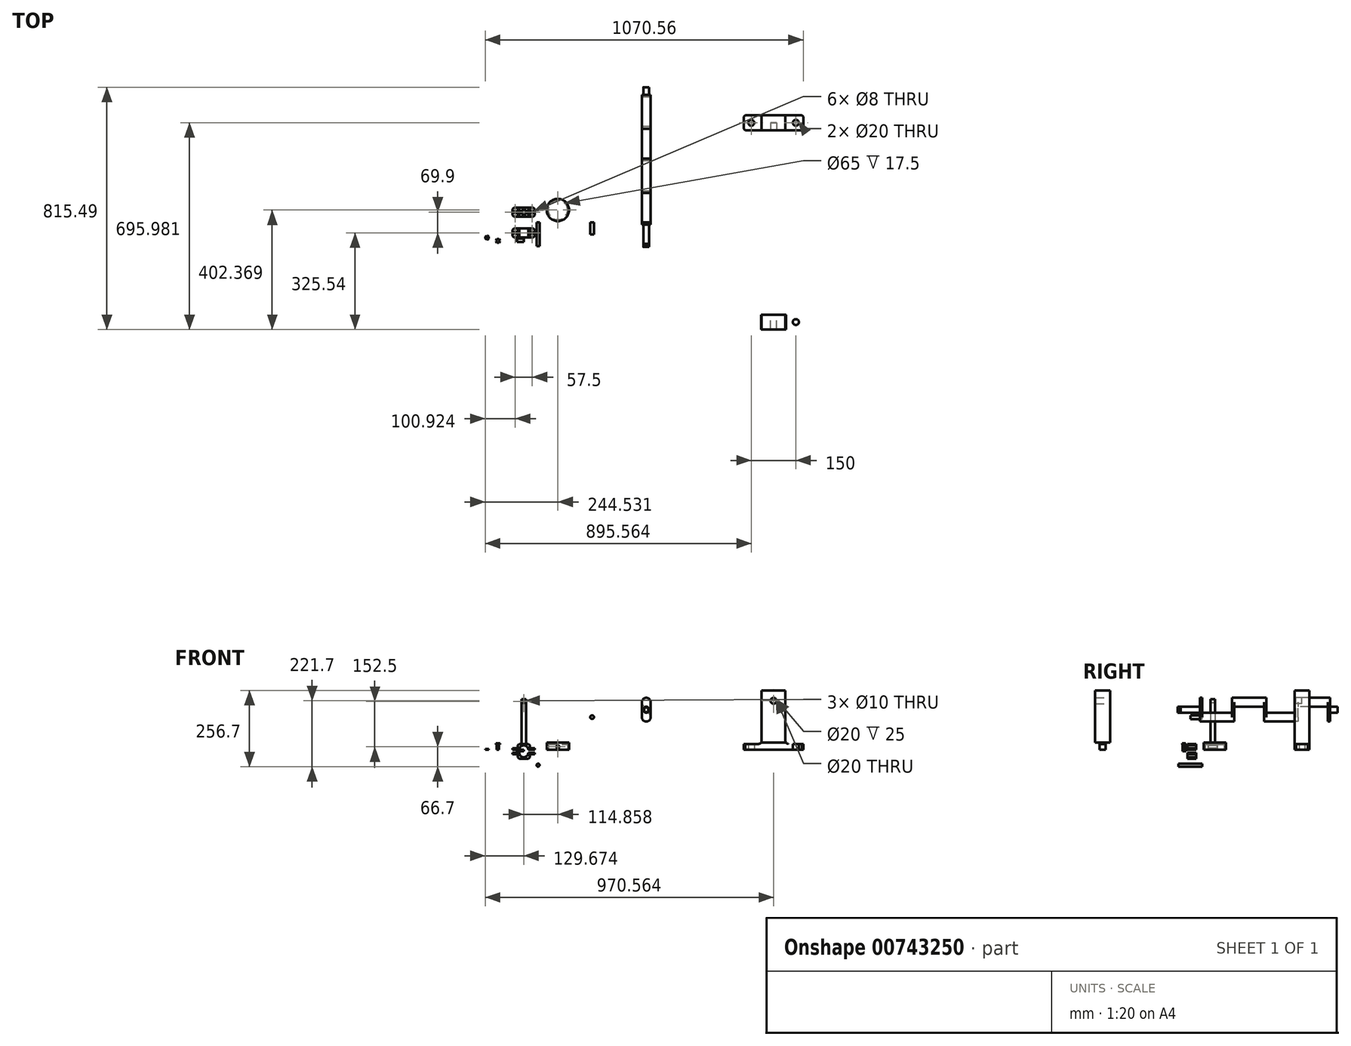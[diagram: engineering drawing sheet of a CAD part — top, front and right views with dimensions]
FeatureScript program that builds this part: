
annotation { "Feature Type Name" : "Feature", "Feature Type Description" : "" }
export const myFeature = defineFeature(function(context is Context, id is Id, definition is map)
    precondition{}
    {
        {
            var Q0;
            Q0=qCreatedBy(makeId("Top.planeOp"),FACE);
            var sketch = newSketch(context, id + "F0", { "sketchPlane" : qUnion([Q0])});
            skLineSegment(sketch, "E0.bottom", {"start": v(-66.46, 49.95) * mm, "end": v(8.54, 49.95) * mm});
            skLineSegment(sketch, "E0.top", {"start": v(-66.46, 19.95) * mm, "end": v(8.54, 19.95) * mm});
            skLineSegment(sketch, "E0.left", {"start": v(-66.46, 49.95) * mm, "end": v(-66.46, 19.95) * mm});
            skLineSegment(sketch, "E0.right", {"start": v(8.54, 49.95) * mm, "end": v(8.54, 19.95) * mm});
            skLineSegment(sketch, "E1", {"start": v(-48.96, 49.95) * mm, "end": v(-48.96, 19.95) * mm});
            skLineSegment(sketch, "E2.MirrorCS", {"start": v(-8.96, 49.95) * mm, "end": v(-8.96, 19.95) * mm});
            skPoint(sketch, "E3.start.orphan", {"position": v(-28.96, 49.95) * mm});
            skCircle(sketch, "E4", {"center": v(-57.7, 34.95) * mm, "radius": 4 * mm});
            skPoint(sketch, "E5.orphan", {"position": v(-48.96, 34.95) * mm});
            skPoint(sketch, "E6.start.orphan", {"position": v(-66.46, 34.95) * mm});
            skLineSegment(sketch, "E7", {"start": v(-28.96, 49.95) * mm, "end": v(-28.96, 38.42) * mm});
            skCircle(sketch, "E8.MirrorC", {"center": v(-0.2, 34.95) * mm, "radius": 4 * mm});
            skSolve(sketch);
        }
        {
            var Q0;
            {var subQ0=sQuery(id+"F0.wireOp",EDGE,"E1");Q0=makeQuery(id+"F0.imprint","IMPRINT",FACE,{"disambiguationData":[TD([[makeQuery(id+"F0.imprint","IMPRINT",EDGE,{"derivedFrom":subQ0}),1.0]])]});}
            extrude(context, id + "F1", {"entities" : qUnion([Q0]), "depth" : 20 * mm, "offsetDistance" : 25 * mm});
        }
        {
            var Q0;
            Q0 = qSketchRegion(id + "F0", true);
            var Q1;
            Q1=makeQuery(id+"F1.opExtrude","CAP_FACE",FACE,{"disambiguationData":[OSD([sQuery(id+"F0.wireOp",EDGE,"E0.bottom"),sQuery(id+"F0.wireOp",EDGE,"E0.top"),sQuery(id+"F0.wireOp",EDGE,"E1"),sQuery(id+"F0.wireOp",EDGE,"E2.MirrorCS")])],"isStart":true});
            extrude(context, id + "F2", {"entities" : qUnion([Q0, Q1]), "operationType" : NewBodyOperationType.ADD, "depth" : 5 * mm, "offsetDistance" : 25 * mm});
        }
        {
            var Q0;
            {var subQ0=sQuery(id+"F0.wireOp",EDGE,"E0.top");var subQ2=makeQuery(id+"F0.imprint","INTERSECT",VERTEX,{"derivedFrom":[subQ0,sQuery(id+"F0.wireOp",EDGE,"E1")]});Q0=makeQuery(id+"F2.boolean.opBoolean","MERGE",FACE,{"derivedFrom":[makeQuery(id+"F1.opExtrude","SWEPT_FACE",FACE,{"disambiguationData":[OSD([subQ0])]}),makeQuery(id+"F2.opExtrude","SWEPT_FACE",FACE,{"disambiguationData":[OSD([subQ0]),TDD([makeQuery(id+"F0.imprint","IMPRINT",EDGE,{"disambiguationData":[TD([[makeQuery(id+"F0.imprint","INTERSECT",VERTEX,{"derivedFrom":[subQ0,sQuery(id+"F0.wireOp",EDGE,"E0.left")]}),-1.0]])],"derivedFrom":subQ0}),makeQuery(id+"F0.imprint","IMPRINT",EDGE,{"disambiguationData":[TD([[subQ2,-1.0]])],"derivedFrom":subQ0}),makeQuery(id+"F0.imprint","IMPRINT",EDGE,{"disambiguationData":[TD([[makeQuery(id+"F0.imprint","INTERSECT",VERTEX,{"derivedFrom":[subQ0,sQuery(id+"F0.wireOp",EDGE,"E0.right")]}),1.0]])],"derivedFrom":subQ0})])]})]});}
            var sketch = newSketch(context, id + "F3", { "sketchPlane" : qUnion([Q0])});
            skLineSegment(sketch, "E9", {"start": v(-28.96, 0) * mm, "end": v(-43.96, 0) * mm});
            skLineSegment(sketch, "E10", {"start": v(-28.96, 0) * mm, "end": v(-28.96, 15) * mm});
            skArc(sketch, "E11", {"start": v(-28.96, 15) * mm, "mid": v(-39.56, 10.6) * mm, "end": v(-43.96, 0) * mm});
            skArc(sketch, "E12.MirrorCS", {"start": v(-28.96, 15) * mm, "mid": v(-18.35, 10.6) * mm, "end": v(-13.96, 0) * mm});
            skSolve(sketch);
        }
        {
            var Q0;
            Q0=makeQuery(id+"F3.imprint","IMPRINT",FACE,{"disambiguationData":[TD([[makeQuery(id+"F3.imprint","IMPRINT",EDGE,{"derivedFrom":sQuery(id+"F3.wireOp",EDGE,"E9")}),1.0]])]});
            var Q1;
            {var subQ0=sQuery(id+"F3.wireOp",EDGE,"E10");Q1=makeQuery(id+"F3.imprint","IMPRINT",FACE,{"disambiguationData":[TD([[makeQuery(id+"F3.imprint","IMPRINT",EDGE,{"derivedFrom":subQ0}),-1.0]])]});}
            extrude(context, id + "F4", {"entities" : qUnion([Q0, Q1]), "operationType" : NewBodyOperationType.REMOVE, "oppositeDirection" : true, "depth" : 46.2 * mm, "offsetDistance" : 25 * mm});
        }
        {
            var Q0;
            Q0=makeQuery(id+"F2.boolean.opBoolean","INTERSECT",EDGE,{"derivedFrom":[makeQuery(id+"F1.opExtrude","SWEPT_FACE",FACE,{"disambiguationData":[OSD([sQuery(id+"F0.wireOp",EDGE,"E1")])]}),makeQuery(id+"F2.opExtrude","CAP_FACE",FACE,{"disambiguationData":[OSD([sQuery(id+"F0.wireOp",EDGE,"E0.bottom"),sQuery(id+"F0.wireOp",EDGE,"E0.top"),sQuery(id+"F0.wireOp",EDGE,"E0.left"),sQuery(id+"F0.wireOp",EDGE,"E0.right"),sQuery(id+"F0.wireOp",EDGE,"E4"),sQuery(id+"F0.wireOp",EDGE,"E8.MirrorC")])],"isStart":false})]});
            var Q1;
            Q1=makeQuery(id+"F2.boolean.opBoolean","INTERSECT",EDGE,{"derivedFrom":[makeQuery(id+"F1.opExtrude","SWEPT_FACE",FACE,{"disambiguationData":[OSD([sQuery(id+"F0.wireOp",EDGE,"E2.MirrorCS")])]}),makeQuery(id+"F2.opExtrude","CAP_FACE",FACE,{"disambiguationData":[OSD([sQuery(id+"F0.wireOp",EDGE,"E0.bottom"),sQuery(id+"F0.wireOp",EDGE,"E0.top"),sQuery(id+"F0.wireOp",EDGE,"E0.left"),sQuery(id+"F0.wireOp",EDGE,"E0.right"),sQuery(id+"F0.wireOp",EDGE,"E4"),sQuery(id+"F0.wireOp",EDGE,"E8.MirrorC")])],"isStart":false})]});
            fillet(context, id + "F5", {"entities" : qUnion([Q0, Q1]), "radius" : 3 * mm, "tangentPropagation" : true, "allowEdgeOverflow" : false});
        }
        {
            var Q0;
            Q0=makeQuery(id+"F1.opExtrude","CAP_EDGE",EDGE,{"disambiguationData":[OSD([sQuery(id+"F0.wireOp",EDGE,"E2.MirrorCS")])],"isStart":false});
            var Q1;
            Q1=makeQuery(id+"F1.opExtrude","CAP_EDGE",EDGE,{"disambiguationData":[OSD([sQuery(id+"F0.wireOp",EDGE,"E1")])],"isStart":false});
            chamfer(context, id + "F6", {"entities" : qUnion([Q0, Q1]), "width" : 5 * mm, "tangentPropagation" : true});
        }
        {
            var Q0;
            Q0=makeQuery(id+"F2.opExtrude","SWEPT_EDGE",EDGE,{"disambiguationData":[OSD([sQuery(id+"F0.wireOp",EDGE,"E0.top"),sQuery(id+"F0.wireOp",EDGE,"E0.left")])]});
            var Q1;
            Q1=makeQuery(id+"F2.opExtrude","SWEPT_EDGE",EDGE,{"disambiguationData":[OSD([sQuery(id+"F0.wireOp",EDGE,"E0.bottom"),sQuery(id+"F0.wireOp",EDGE,"E0.left")])]});
            var Q2;
            Q2=makeQuery(id+"F2.opExtrude","SWEPT_EDGE",EDGE,{"disambiguationData":[OSD([sQuery(id+"F0.wireOp",EDGE,"E0.bottom"),sQuery(id+"F0.wireOp",EDGE,"E0.right")])]});
            var Q3;
            Q3=makeQuery(id+"F2.opExtrude","SWEPT_EDGE",EDGE,{"disambiguationData":[OSD([sQuery(id+"F0.wireOp",EDGE,"E0.top"),sQuery(id+"F0.wireOp",EDGE,"E0.right")])]});
            chamfer(context, id + "F7", {"entities" : qUnion([Q0, Q1, Q2, Q3]), "width" : 5 * mm, "tangentPropagation" : true});
        }
        {
            var Q0;
            Q0=makeQuery(id+"F1.opExtrude","SWEPT_BODY",BODY,{"disambiguationData":[OSD([sQuery(id+"F0.wireOp",EDGE,"E0.bottom"),sQuery(id+"F0.wireOp",EDGE,"E0.top"),sQuery(id+"F0.wireOp",EDGE,"E1"),sQuery(id+"F0.wireOp",EDGE,"E2.MirrorCS")])]});
            var Q1;
            Q1=qCreatedBy(makeId("Front.planeOp"),FACE);
            mirror(context, id + "F8", {"entities" : qUnion([Q0]), "mirrorPlane" : qUnion([Q1])});
        }
        {
            var Q0;
            Q0=makeQuery(id+"F1.opExtrude","CAP_FACE",FACE,{"disambiguationData":[OSD([sQuery(id+"F0.wireOp",EDGE,"E0.bottom"),sQuery(id+"F0.wireOp",EDGE,"E0.top"),sQuery(id+"F0.wireOp",EDGE,"E1"),sQuery(id+"F0.wireOp",EDGE,"E2.MirrorCS")])],"isStart":false});
            var sketch = newSketch(context, id + "F9", { "sketchPlane" : qUnion([Q0])});
            skLineSegment(sketch, "E13", {"start": v(-43.96, 34.95) * mm, "end": v(-13.96, 34.95) * mm});
            skCircle(sketch, "E14.cCircle", {"center": v(-28.96, 34.95) * mm, "radius": 7.5 * mm, "construction": true});
            skLineSegment(sketch, "E14.0", {"start": v(-36.46, 27.45) * mm, "end": v(-36.46, 42.45) * mm});
            skLineSegment(sketch, "E14.1", {"start": v(-36.46, 42.45) * mm, "end": v(-21.46, 42.45) * mm});
            skLineSegment(sketch, "E14.2", {"start": v(-21.46, 42.45) * mm, "end": v(-21.46, 27.45) * mm});
            skLineSegment(sketch, "E14.3", {"start": v(-21.46, 27.45) * mm, "end": v(-36.46, 27.45) * mm});
            skPoint(sketch, "E14.0.midPoint", {"position": v(-36.46, 34.95) * mm});
            skSolve(sketch);
        }
        {
            var Q0;
            {var subQ5=sQuery(id+"F9.wireOp",EDGE,"E14.3");Q0=makeQuery(id+"F9.imprint","IMPRINT",FACE,{"disambiguationData":[TD([[makeQuery(id+"F9.imprint","IMPRINT",EDGE,{"derivedFrom":subQ5}),-1.0]])]});}
            var Q1;
            {var subQ5=sQuery(id+"F9.wireOp",EDGE,"E14.1");Q1=makeQuery(id+"F9.imprint","IMPRINT",FACE,{"disambiguationData":[TD([[makeQuery(id+"F9.imprint","IMPRINT",EDGE,{"derivedFrom":subQ5}),-1.0]])]});}
            extrude(context, id + "F10", {"entities" : qUnion([Q0, Q1]), "operationType" : NewBodyOperationType.ADD, "depth" : 150 * mm, "offsetDistance" : 25 * mm});
        }
        {
            var Q0;
            Q0=makeQuery(id+"F10.opExtrude","SWEPT_FACE",FACE,{"disambiguationData":[OSD([sQuery(id+"F9.wireOp",EDGE,"E14.3")])]});
            var sketch = newSketch(context, id + "F11", { "sketchPlane" : qUnion([Q0])});
            skLineSegment(sketch, "E15", {"start": v(-28.96, 170) * mm, "end": v(-28.96, 162.5) * mm});
            skCircle(sketch, "E16", {"center": v(-28.96, 162.5) * mm, "radius": 5 * mm});
            skSolve(sketch);
        }
        {
            var Q0;
            Q0=makeQuery(id+"F11.imprint","IMPRINT",FACE,{"disambiguationData":[TD([[makeQuery(id+"F11.imprint","IMPRINT",EDGE,{"derivedFrom":sQuery(id+"F11.wireOp",EDGE,"E16")}),1.0]])]});
            extrude(context, id + "F12", {"entities" : qUnion([Q0]), "operationType" : NewBodyOperationType.REMOVE, "oppositeDirection" : true, "depth" : 25 * mm, "offsetDistance" : 25 * mm});
        }
        {
            var Q0;
            Q0=qCreatedBy(makeId("Top.planeOp"),FACE);
            var sketch = newSketch(context, id + "F13", { "sketchPlane" : qUnion([Q0])});
            skCircle(sketch, "E17", {"center": v(85.9, 41.88) * mm, "radius": 37.5 * mm});
            skSolve(sketch);
        }
        {
            var Q0;
            Q0=makeQuery(id+"F13.imprint","IMPRINT",FACE,{"disambiguationData":[TD([[makeQuery(id+"F13.imprint","IMPRINT",EDGE,{"derivedFrom":sQuery(id+"F13.wireOp",EDGE,"E17")}),1.0]])]});
            extrude(context, id + "F14", {"entities" : qUnion([Q0]), "depth" : 25 * mm, "offsetDistance" : 25 * mm});
        }
        {
            var Q0;
            Q0=makeQuery(id+"F14.opExtrude","CAP_FACE",FACE,{"disambiguationData":[OSD([sQuery(id+"F13.wireOp",EDGE,"E17")])],"isStart":true});
            var sketch = newSketch(context, id + "F15", { "sketchPlane" : qUnion([Q0])});
            skCircle(sketch, "E18", {"center": v(85.9, -41.88) * mm, "radius": 32.5 * mm});
            skSolve(sketch);
        }
        {
            var Q0;
            Q0=makeQuery(id+"F15.imprint","IMPRINT",FACE,{"disambiguationData":[TD([[makeQuery(id+"F15.imprint","IMPRINT",EDGE,{"derivedFrom":sQuery(id+"F15.wireOp",EDGE,"E18")}),1.0]])]});
            extrude(context, id + "F16", {"entities" : qUnion([Q0]), "operationType" : NewBodyOperationType.REMOVE, "oppositeDirection" : true, "depth" : 17.5 * mm, "offsetDistance" : 25 * mm});
        }
        {
            var Q0;
            Q0=makeQuery(id+"F16.boolean.opBoolean","COPY",FACE,{"derivedFrom":makeQuery(id+"F16.opExtrude","CAP_FACE",FACE,{"disambiguationData":[OSD([sQuery(id+"F15.wireOp",EDGE,"E18")])],"isStart":false})});
            var sketch = newSketch(context, id + "F17", { "sketchPlane" : qUnion([Q0])});
            skLineSegment(sketch, "E19.0", {"start": v(97.9, -53.88) * mm, "end": v(73.9, -53.88) * mm});
            skLineSegment(sketch, "E19.1", {"start": v(73.9, -53.88) * mm, "end": v(73.9, -29.88) * mm});
            skLineSegment(sketch, "E19.2", {"start": v(73.9, -29.88) * mm, "end": v(97.9, -29.88) * mm});
            skLineSegment(sketch, "E19.3", {"start": v(97.9, -29.88) * mm, "end": v(97.9, -53.88) * mm});
            skPoint(sketch, "E19.0.midPoint", {"position": v(85.9, -53.88) * mm});
            skPoint(sketch, "E19.cCircle.center.orphan", {"position": v(85.9, -41.88) * mm});
            skSolve(sketch);
        }
        {
            var Q0;
            Q0 = qSketchRegion(id + "F17", true);
            extrude(context, id + "F18", {"entities" : qUnion([Q0]), "operationType" : NewBodyOperationType.ADD, "depth" : 15 * mm, "offsetDistance" : 25 * mm});
        }
        {
            var Q0;
            Q0=makeQuery(id+"F18.opExtrude","SWEPT_FACE",FACE,{"disambiguationData":[OSD([sQuery(id+"F17.wireOp",EDGE,"E19.0")])]});
            var sketch = newSketch(context, id + "F19", { "sketchPlane" : qUnion([Q0])});
            skLineSegment(sketch, "E20", {"start": v(-85.9, 2.5) * mm, "end": v(-85.9, 17.5) * mm});
            skCircle(sketch, "E21", {"center": v(-85.9, 10) * mm, "radius": 5 * mm});
            skSolve(sketch);
        }
        {
            var Q0;
            {var subQ0=sQuery(id+"F19.wireOp",EDGE,"E21");var subQ1=sQuery(id+"F19.wireOp",EDGE,"E20");var subQ2=makeQuery(id+"F19.imprint","INTERSECT",VERTEX,{"disambiguationData":[OD(0.0)],"derivedFrom":[subQ1,subQ0]});Q0=makeQuery(id+"F19.imprint","IMPRINT",FACE,{"disambiguationData":[TD([[makeQuery(id+"F19.imprint","IMPRINT",EDGE,{"disambiguationData":[TD([[subQ2,-1.0]])],"derivedFrom":subQ1}),1.0]])]});}
            var Q1;
            {var subQ0=sQuery(id+"F19.wireOp",EDGE,"E21");var subQ1=sQuery(id+"F19.wireOp",EDGE,"E20");var subQ2=makeQuery(id+"F19.imprint","INTERSECT",VERTEX,{"disambiguationData":[OD(0.0)],"derivedFrom":[subQ1,subQ0]});Q1=makeQuery(id+"F19.imprint","IMPRINT",FACE,{"disambiguationData":[TD([[makeQuery(id+"F19.imprint","IMPRINT",EDGE,{"disambiguationData":[TD([[subQ2,-1.0]])],"derivedFrom":subQ1}),-1.0]])]});}
            extrude(context, id + "F20", {"entities" : qUnion([Q0, Q1]), "operationType" : NewBodyOperationType.REMOVE, "oppositeDirection" : true, "depth" : 101.7 * mm, "offsetDistance" : 25 * mm});
        }
        {
            var Q0;
            Q0 = qSketchRegion(id + "F19", true);
            extrude(context, id + "F21", {"entities" : qUnion([Q0]), "operationType" : NewBodyOperationType.REMOVE, "oppositeDirection" : true, "depth" : -50 * mm, "offsetDistance" : 25 * mm});
        }
        {
            var Q0;
            Q0=makeQuery(id+"F18.opExtrude","SWEPT_FACE",FACE,{"disambiguationData":[OSD([sQuery(id+"F17.wireOp",EDGE,"E19.3")])]});
            var sketch = newSketch(context, id + "F22", { "sketchPlane" : qUnion([Q0])});
            skLineSegment(sketch, "E22.bottom", {"start": v(53.88, 2.5) * mm, "end": v(29.88, 2.5) * mm});
            skLineSegment(sketch, "E22.top", {"start": v(53.88, 17.5) * mm, "end": v(29.88, 17.5) * mm});
            skLineSegment(sketch, "E22.left", {"start": v(53.88, 2.5) * mm, "end": v(53.88, 17.5) * mm});
            skLineSegment(sketch, "E22.right", {"start": v(29.88, 2.5) * mm, "end": v(29.88, 17.5) * mm});
            skSolve(sketch);
        }
        {
            var Q0;
            Q0 = qSketchRegion(id + "F22", true);
            extrude(context, id + "F23", {"entities" : qUnion([Q0]), "operationType" : NewBodyOperationType.REMOVE, "oppositeDirection" : true, "depth" : 27.8 * mm, "offsetDistance" : 25 * mm});
        }
        {
            var Q0;
            Q0=qCreatedBy(makeId("Front.planeOp"),FACE);
            var sketch = newSketch(context, id + "F24", { "sketchPlane" : qUnion([Q0])});
            skCircle(sketch, "E23", {"center": v(19.1, -51.7) * mm, "radius": 5 * mm});
            skSolve(sketch);
        }
        {
            var Q0;
            Q0 = qSketchRegion(id + "F24", true);
            extrude(context, id + "F25", {"entities" : qUnion([Q0]), "depth" : 80 * mm, "offsetDistance" : 25 * mm});
        }
        {
            var Q0;
            Q0=qCreatedBy(makeId("Top.planeOp"),FACE);
            var sketch = newSketch(context, id + "F26", { "sketchPlane" : qUnion([Q0])});
            skCircle(sketch, "E24", {"center": v(-115.98, -62.01) * mm, "radius": 4 * mm});
            skLineSegment(sketch, "E25", {"start": v(-116.37, -51.4) * mm, "end": v(-136.85, -51.4) * mm});
            skLineSegment(sketch, "E26", {"start": v(-136.85, -51.4) * mm, "end": v(-136.85, -57.16) * mm});
            skPoint(sketch, "E27", {"position": v(-152.63, -51.4) * mm});
            skCircle(sketch, "E28", {"center": v(-152.63, -51.4) * mm, "radius": 4 * mm});
            skCircle(sketch, "E29.cCircle", {"center": v(-152.63, -51.4) * mm, "radius": 6 * mm, "construction": true});
            skLineSegment(sketch, "E29.0", {"start": v(-146.63, -47.93) * mm, "end": v(-146.63, -54.86) * mm});
            skLineSegment(sketch, "E29.1", {"start": v(-146.63, -54.86) * mm, "end": v(-152.63, -58.32) * mm});
            skLineSegment(sketch, "E29.2", {"start": v(-152.63, -58.32) * mm, "end": v(-158.63, -54.86) * mm});
            skLineSegment(sketch, "E29.3", {"start": v(-158.63, -54.86) * mm, "end": v(-158.63, -47.93) * mm});
            skLineSegment(sketch, "E29.4", {"start": v(-158.63, -47.93) * mm, "end": v(-152.63, -44.46) * mm});
            skLineSegment(sketch, "E29.5", {"start": v(-152.63, -44.46) * mm, "end": v(-146.63, -47.93) * mm});
            skPoint(sketch, "E29.0.midPoint", {"position": v(-146.63, -51.4) * mm});
            skSolve(sketch);
        }
        {
            var Q0;
            Q0=makeQuery(id+"F26.imprint","IMPRINT",FACE,{"disambiguationData":[TD([[makeQuery(id+"F26.imprint","IMPRINT",EDGE,{"derivedFrom":sQuery(id+"F26.wireOp",EDGE,"E24")}),1.0]])]});
            extrude(context, id + "F27", {"entities" : qUnion([Q0]), "depth" : 17.5 * mm, "offsetDistance" : 25 * mm});
        }
        {
            var Q0;
            Q0=makeQuery(id+"F27.opExtrude","CAP_FACE",FACE,{"disambiguationData":[OSD([sQuery(id+"F26.wireOp",EDGE,"E24")])],"isStart":false});
            var sketch = newSketch(context, id + "F28", { "sketchPlane" : qUnion([Q0])});
            skCircle(sketch, "E30.cCircle", {"center": v(-115.98, -62.01) * mm, "radius": 6 * mm, "construction": true});
            skLineSegment(sketch, "E30.0", {"start": v(-112.51, -68.01) * mm, "end": v(-119.44, -68.01) * mm});
            skLineSegment(sketch, "E30.1", {"start": v(-119.44, -68.01) * mm, "end": v(-122.9, -62.01) * mm});
            skLineSegment(sketch, "E30.2", {"start": v(-122.9, -62.01) * mm, "end": v(-119.44, -56.01) * mm});
            skLineSegment(sketch, "E30.3", {"start": v(-119.44, -56.01) * mm, "end": v(-112.51, -56.01) * mm});
            skLineSegment(sketch, "E30.4", {"start": v(-112.51, -56.01) * mm, "end": v(-109.05, -62.01) * mm});
            skLineSegment(sketch, "E30.5", {"start": v(-109.05, -62.01) * mm, "end": v(-112.51, -68.01) * mm});
            skPoint(sketch, "E30.0.midPoint", {"position": v(-115.98, -68.01) * mm});
            skSolve(sketch);
        }
        {
            var Q0;
            Q0=makeQuery(id+"F28.imprint","IMPRINT",FACE,{"disambiguationData":[TD([[makeQuery(id+"F28.imprint","IMPRINT",EDGE,{"derivedFrom":sQuery(id+"F28.wireOp",EDGE,"E30.0")}),-1.0]])]});
            var Q1;
            Q1=makeQuery(id+"F28.imprint","IMPRINT",FACE,{"disambiguationData":[TD([[makeQuery(id+"F28.imprint","IMPRINT",EDGE,{"derivedFrom":makeQuery(id+"F27.opExtrude","CAP_EDGE",EDGE,{"disambiguationData":[OSD([sQuery(id+"F26.wireOp",EDGE,"E24")])],"isStart":false})}),1.0]])]});
            extrude(context, id + "F29", {"entities" : qUnion([Q0, Q1]), "operationType" : NewBodyOperationType.ADD, "depth" : 4 * mm, "offsetDistance" : 25 * mm});
        }
        {
            var Q0;
            Q0=makeQuery(id+"F26.imprint","IMPRINT",FACE,{"disambiguationData":[TD([[makeQuery(id+"F26.imprint","IMPRINT",EDGE,{"derivedFrom":sQuery(id+"F26.wireOp",EDGE,"E28")}),-1.0]])]});
            extrude(context, id + "F30", {"entities" : qUnion([Q0]), "depth" : 3 * mm, "offsetDistance" : 25 * mm});
        }
        {
            var Q0;
            Q0=qCreatedBy(makeId("Top.planeOp"),FACE);
            var sketch = newSketch(context, id + "F31", { "sketchPlane" : qUnion([Q0])});
            skLineSegment(sketch, "E31.bottom", {"start": v(-51.99, -65.98) * mm, "end": v(-28.68, -65.98) * mm});
            skLineSegment(sketch, "E31.top", {"start": v(-51.99, -54.32) * mm, "end": v(-28.68, -54.32) * mm});
            skLineSegment(sketch, "E31.left", {"start": v(-51.99, -65.98) * mm, "end": v(-51.99, -54.32) * mm});
            skLineSegment(sketch, "E31.right", {"start": v(-28.68, -65.98) * mm, "end": v(-28.68, -54.32) * mm});
            skSolve(sketch);
        }
        {
            var Q0;
            Q0=makeQuery(id+"F31.imprint","IMPRINT",FACE,{"disambiguationData":[TD([[makeQuery(id+"F31.imprint","IMPRINT",EDGE,{"derivedFrom":sQuery(id+"F31.wireOp",EDGE,"E31.bottom")}),1.0]])]});
            extrude(context, id + "F32", {"entities" : qUnion([Q0]), "depth" : -5 * mm, "offsetDistance" : 25 * mm});
        }
        {
            var Q0;
            Q0=makeQuery(id+"F8.opPattern","COPY",BODY,{"derivedFrom":makeQuery(id+"F1.opExtrude","SWEPT_BODY",BODY,{"disambiguationData":[OSD([sQuery(id+"F0.wireOp",EDGE,"E0.bottom"),sQuery(id+"F0.wireOp",EDGE,"E0.top"),sQuery(id+"F0.wireOp",EDGE,"E1"),sQuery(id+"F0.wireOp",EDGE,"E2.MirrorCS")])]}),"instanceName":"1"});
            var Q1;
            Q1=makeQuery(id+"F32.opExtrude","CAP_FACE",FACE,{"disambiguationData":[OSD([sQuery(id+"F31.wireOp",EDGE,"E31.bottom"),sQuery(id+"F31.wireOp",EDGE,"E31.top"),sQuery(id+"F31.wireOp",EDGE,"E31.left"),sQuery(id+"F31.wireOp",EDGE,"E31.right")])],"isStart":false});
            mirror(context, id + "F33", {"entities" : qUnion([Q0]), "mirrorPlane" : qUnion([Q1])});
        }
        {
            var Q0;
            Q0=qCreatedBy(makeId("Front.planeOp"),FACE);
            var sketch = newSketch(context, id + "F34", { "sketchPlane" : qUnion([Q0])});
            skCircle(sketch, "E32", {"center": v(383.3, 110.18) * mm, "radius": 15 * mm});
            skLineSegment(sketch, "E33", {"start": v(383.3, 110.18) * mm, "end": v(398.3, 110.18) * mm});
            skLineSegment(sketch, "E34", {"start": v(398.3, 110.18) * mm, "end": v(398.3, 160.18) * mm});
            skLineSegment(sketch, "E35", {"start": v(383.3, 110.18) * mm, "end": v(383.3, 125.18) * mm});
            skLineSegment(sketch, "E36.MirrorCS", {"start": v(368.3, 110.18) * mm, "end": v(368.3, 160.18) * mm});
            skArc(sketch, "E37", {"start": v(398.3, 160.18) * mm, "mid": v(383.3, 175.18) * mm, "end": v(368.3, 160.18) * mm});
            skSolve(sketch);
        }
        {
            var Q0;
            Q0 = qSketchRegion(id + "F34", true);
            extrude(context, id + "F35", {"entities" : qUnion([Q0]), "depth" : 7.5 * mm, "offsetDistance" : 25 * mm});
        }
        {
            var Q0;
            Q0=makeQuery(id+"F35.opExtrude","CAP_FACE",FACE,{"disambiguationData":[OSD([sQuery(id+"F34.wireOp",EDGE,"E32"),sQuery(id+"F34.wireOp",EDGE,"E34"),sQuery(id+"F34.wireOp",EDGE,"E36.MirrorCS"),sQuery(id+"F34.wireOp",EDGE,"E37")])],"isStart":true});
            var sketch = newSketch(context, id + "F36", { "sketchPlane" : qUnion([Q0])});
            skLineSegment(sketch, "E38", {"start": v(-383.3, 95.18) * mm, "end": v(-383.3, 110.18) * mm});
            skCircle(sketch, "E39", {"center": v(-383.3, 110.18) * mm, "radius": 15 * mm});
            skSolve(sketch);
        }
        {
            var Q0;
            Q0 = qSketchRegion(id + "F36", true);
            extrude(context, id + "F37", {"entities" : qUnion([Q0]), "operationType" : NewBodyOperationType.ADD, "depth" : 100 * mm, "offsetDistance" : 25 * mm});
        }
        {
            var Q0;
            Q0=makeQuery(id+"F37.opExtrude","CAP_FACE",FACE,{"disambiguationData":[OSD([sQuery(id+"F36.wireOp",EDGE,"E39")])],"isStart":false});
            var sketch = newSketch(context, id + "F38", { "sketchPlane" : qUnion([Q0])});
            skLineSegment(sketch, "E40", {"start": v(-383.3, 110.18) * mm, "end": v(-398.3, 110.18) * mm});
            skLineSegment(sketch, "E41", {"start": v(-398.3, 110.18) * mm, "end": v(-398.3, 160.18) * mm});
            skLineSegment(sketch, "E42", {"start": v(-383.3, 110.18) * mm, "end": v(-383.3, 125.18) * mm});
            skLineSegment(sketch, "E43.MirrorCS", {"start": v(-368.3, 110.18) * mm, "end": v(-368.3, 160.18) * mm});
            skArc(sketch, "E44", {"start": v(-368.3, 160.18) * mm, "mid": v(-383.3, 175.18) * mm, "end": v(-398.3, 160.18) * mm});
            skPoint(sketch, "E45.end.orphan", {"position": v(-367.15, 110.18) * mm});
            skArc(sketch, "E46", {"start": v(-398.3, 110.18) * mm, "mid": v(-383.3, 95.18) * mm, "end": v(-368.3, 110.18) * mm});
            skSolve(sketch);
        }
        {
            var Q0;
            Q0 = qSketchRegion(id + "F38", true);
            extrude(context, id + "F39", {"entities" : qUnion([Q0]), "operationType" : NewBodyOperationType.ADD, "depth" : 7.5 * mm, "offsetDistance" : 25 * mm});
        }
        {
            var Q0;
            Q0=makeQuery(id+"F39.opExtrude","CAP_FACE",FACE,{"disambiguationData":[OSD([sQuery(id+"F38.wireOp",EDGE,"E41"),sQuery(id+"F38.wireOp",EDGE,"E43.MirrorCS"),sQuery(id+"F38.wireOp",EDGE,"E44"),sQuery(id+"F38.wireOp",EDGE,"E46")])],"isStart":false});
            var sketch = newSketch(context, id + "F40", { "sketchPlane" : qUnion([Q0])});
            skCircle(sketch, "E47", {"center": v(-383.3, 160.18) * mm, "radius": 15 * mm});
            skSolve(sketch);
        }
        {
            var Q0;
            Q0 = qSketchRegion(id + "F40", true);
            extrude(context, id + "F41", {"entities" : qUnion([Q0]), "operationType" : NewBodyOperationType.ADD, "depth" : 100 * mm, "offsetDistance" : 25 * mm});
        }
        {
            var Q0;
            Q0=makeQuery(id+"F41.opExtrude","CAP_FACE",FACE,{"disambiguationData":[OSD([sQuery(id+"F40.wireOp",EDGE,"E47")])],"isStart":false});
            var sketch = newSketch(context, id + "F42", { "sketchPlane" : qUnion([Q0])});
            skLineSegment(sketch, "E48", {"start": v(-383.3, 160.18) * mm, "end": v(-398.3, 160.18) * mm});
            skLineSegment(sketch, "E49", {"start": v(-398.3, 160.18) * mm, "end": v(-398.3, 110.18) * mm});
            skLineSegment(sketch, "E50", {"start": v(-383.3, 160.18) * mm, "end": v(-383.3, 145.18) * mm});
            skLineSegment(sketch, "E51.MirrorCS", {"start": v(-368.3, 160.18) * mm, "end": v(-368.3, 110.18) * mm});
            skArc(sketch, "E52", {"start": v(-368.3, 160.18) * mm, "mid": v(-383.3, 175.18) * mm, "end": v(-398.3, 160.18) * mm});
            skArc(sketch, "E53", {"start": v(-398.3, 110.18) * mm, "mid": v(-383.3, 95.18) * mm, "end": v(-368.3, 110.18) * mm});
            skSolve(sketch);
        }
        {
            var Q0;
            {var subQ2=sQuery(id+"F42.wireOp",EDGE,"E49");Q0=makeQuery(id+"F42.imprint","IMPRINT",FACE,{"disambiguationData":[TD([[makeQuery(id+"F42.imprint","IMPRINT",EDGE,{"derivedFrom":subQ2}),1.0]])]});}
            var Q1;
            Q1=makeQuery(id+"F42.imprint","IMPRINT",FACE,{"disambiguationData":[TD([[makeQuery(id+"F42.imprint","IMPRINT",EDGE,{"derivedFrom":sQuery(id+"F42.wireOp",EDGE,"E48")}),-1.0]])]});
            var Q2;
            {var subQ0=sQuery(id+"F42.wireOp",EDGE,"E48");Q2=makeQuery(id+"F42.imprint","IMPRINT",FACE,{"disambiguationData":[TD([[makeQuery(id+"F42.imprint","IMPRINT",EDGE,{"derivedFrom":subQ0}),1.0]])]});}
            extrude(context, id + "F43", {"entities" : qUnion([Q0, Q1, Q2]), "operationType" : NewBodyOperationType.ADD, "depth" : 7.5 * mm, "offsetDistance" : 25 * mm});
        }
        {
            var Q0;
            Q0=makeQuery(id+"F43.opExtrude","CAP_FACE",FACE,{"disambiguationData":[OSD([sQuery(id+"F42.wireOp",EDGE,"E49"),sQuery(id+"F42.wireOp",EDGE,"E51.MirrorCS"),sQuery(id+"F42.wireOp",EDGE,"E52"),sQuery(id+"F42.wireOp",EDGE,"E53")])],"isStart":false});
            var sketch = newSketch(context, id + "F44", { "sketchPlane" : qUnion([Q0])});
            skCircle(sketch, "E54", {"center": v(-383.3, 110.18) * mm, "radius": 15 * mm});
            skSolve(sketch);
        }
        {
            var Q0;
            Q0 = qSketchRegion(id + "F44", true);
            extrude(context, id + "F45", {"entities" : qUnion([Q0]), "operationType" : NewBodyOperationType.ADD, "depth" : 100 * mm, "offsetDistance" : 25 * mm});
        }
        {
            var Q0;
            Q0=makeQuery(id+"F45.opExtrude","CAP_FACE",FACE,{"disambiguationData":[OSD([sQuery(id+"F44.wireOp",EDGE,"E54")])],"isStart":false});
            var sketch = newSketch(context, id + "F46", { "sketchPlane" : qUnion([Q0])});
            skLineSegment(sketch, "E55", {"start": v(-383.3, 110.18) * mm, "end": v(-398.3, 110.18) * mm});
            skLineSegment(sketch, "E56", {"start": v(-398.3, 110.18) * mm, "end": v(-398.3, 160.18) * mm});
            skLineSegment(sketch, "E57", {"start": v(-383.3, 110.18) * mm, "end": v(-383.3, 125.18) * mm});
            skLineSegment(sketch, "E58.MirrorCS", {"start": v(-368.3, 110.18) * mm, "end": v(-368.3, 160.18) * mm});
            skArc(sketch, "E59", {"start": v(-398.3, 110.18) * mm, "mid": v(-383.3, 95.18) * mm, "end": v(-368.3, 110.18) * mm});
            skArc(sketch, "E60", {"start": v(-368.3, 160.18) * mm, "mid": v(-383.3, 175.18) * mm, "end": v(-398.3, 160.18) * mm});
            skSolve(sketch);
        }
        {
            var Q0;
            Q0 = qSketchRegion(id + "F46", true);
            extrude(context, id + "F47", {"entities" : qUnion([Q0]), "operationType" : NewBodyOperationType.ADD, "depth" : 7.5 * mm, "offsetDistance" : 25 * mm});
        }
        {
            var Q0;
            Q0=makeQuery(id+"F47.opExtrude","CAP_FACE",FACE,{"disambiguationData":[OSD([sQuery(id+"F46.wireOp",EDGE,"E56"),sQuery(id+"F46.wireOp",EDGE,"E58.MirrorCS"),sQuery(id+"F46.wireOp",EDGE,"E59"),sQuery(id+"F46.wireOp",EDGE,"E60")])],"isStart":false});
            var sketch = newSketch(context, id + "F48", { "sketchPlane" : qUnion([Q0])});
            skCircle(sketch, "E61", {"center": v(-383.3, 160.18) * mm, "radius": 15 * mm});
            skSolve(sketch);
        }
        {
            var Q0;
            Q0 = qSketchRegion(id + "F48", true);
            extrude(context, id + "F49", {"entities" : qUnion([Q0]), "operationType" : NewBodyOperationType.ADD, "depth" : 100 * mm, "offsetDistance" : 25 * mm});
        }
        {
            var Q0;
            Q0=makeQuery(id+"F49.opExtrude","CAP_FACE",FACE,{"disambiguationData":[OSD([sQuery(id+"F48.wireOp",EDGE,"E61")])],"isStart":false});
            var sketch = newSketch(context, id + "F50", { "sketchPlane" : qUnion([Q0])});
            skLineSegment(sketch, "E62", {"start": v(-383.3, 160.18) * mm, "end": v(-398.3, 160.18) * mm});
            skLineSegment(sketch, "E63", {"start": v(-398.3, 160.18) * mm, "end": v(-398.3, 110.18) * mm});
            skLineSegment(sketch, "E64", {"start": v(-383.3, 160.18) * mm, "end": v(-383.3, 145.18) * mm});
            skLineSegment(sketch, "E65.MirrorCS", {"start": v(-368.3, 160.18) * mm, "end": v(-368.3, 110.18) * mm});
            skArc(sketch, "E66", {"start": v(-368.3, 160.18) * mm, "mid": v(-383.3, 175.18) * mm, "end": v(-398.3, 160.18) * mm});
            skArc(sketch, "E67", {"start": v(-398.3, 110.18) * mm, "mid": v(-383.3, 95.18) * mm, "end": v(-368.3, 110.18) * mm});
            skSolve(sketch);
        }
        {
            var Q0;
            {var subQ2=sQuery(id+"F50.wireOp",EDGE,"E63");Q0=makeQuery(id+"F50.imprint","IMPRINT",FACE,{"disambiguationData":[TD([[makeQuery(id+"F50.imprint","IMPRINT",EDGE,{"derivedFrom":subQ2}),1.0]])]});}
            var Q1;
            Q1=makeQuery(id+"F50.imprint","IMPRINT",FACE,{"disambiguationData":[TD([[makeQuery(id+"F50.imprint","IMPRINT",EDGE,{"derivedFrom":sQuery(id+"F50.wireOp",EDGE,"E62")}),-1.0]])]});
            var Q2;
            {var subQ0=sQuery(id+"F50.wireOp",EDGE,"E62");Q2=makeQuery(id+"F50.imprint","IMPRINT",FACE,{"disambiguationData":[TD([[makeQuery(id+"F50.imprint","IMPRINT",EDGE,{"derivedFrom":subQ0}),1.0]])]});}
            extrude(context, id + "F51", {"entities" : qUnion([Q0, Q1, Q2]), "operationType" : NewBodyOperationType.ADD, "depth" : 7.5 * mm, "offsetDistance" : 25 * mm});
        }
        {
            var Q0;
            Q0=makeQuery(id+"F51.opExtrude","CAP_FACE",FACE,{"disambiguationData":[OSD([sQuery(id+"F50.wireOp",EDGE,"E63"),sQuery(id+"F50.wireOp",EDGE,"E65.MirrorCS"),sQuery(id+"F50.wireOp",EDGE,"E66"),sQuery(id+"F50.wireOp",EDGE,"E67")])],"isStart":false});
            var sketch = newSketch(context, id + "F52", { "sketchPlane" : qUnion([Q0])});
            skLineSegment(sketch, "E68", {"start": v(-398.3, 135.18) * mm, "end": v(-393.3, 135.18) * mm});
            skCircle(sketch, "E69", {"center": v(-383.3, 135.18) * mm, "radius": 10 * mm});
            skLineSegment(sketch, "E70.trimOffspring", {"start": v(-373.3, 135.18) * mm, "end": v(-368.3, 135.18) * mm});
            skSolve(sketch);
        }
        {
            var Q0;
            {var subQ0=sQuery(id+"F52.wireOp",EDGE,"E69");var subQ1=makeQuery(id+"F52.imprint","INTERSECT",VERTEX,{"derivedFrom":[sQuery(id+"F52.wireOp",EDGE,"E68"),subQ0]});Q0=makeQuery(id+"F52.imprint","IMPRINT",FACE,{"disambiguationData":[TD([[makeQuery(id+"F52.imprint","IMPRINT",EDGE,{"disambiguationData":[TD([[subQ1,1.0]])],"derivedFrom":subQ0}),1.0]])]});}
            extrude(context, id + "F53", {"entities" : qUnion([Q0]), "operationType" : NewBodyOperationType.ADD, "depth" : 25 * mm, "offsetDistance" : 25 * mm});
        }
        {
            var Q0;
            Q0=makeQuery(id+"F35.opExtrude","CAP_FACE",FACE,{"disambiguationData":[OSD([sQuery(id+"F34.wireOp",EDGE,"E32"),sQuery(id+"F34.wireOp",EDGE,"E34"),sQuery(id+"F34.wireOp",EDGE,"E36.MirrorCS"),sQuery(id+"F34.wireOp",EDGE,"E37")])],"isStart":false});
            var sketch = newSketch(context, id + "F54", { "sketchPlane" : qUnion([Q0])});
            skLineSegment(sketch, "E71", {"start": v(368.3, 135.18) * mm, "end": v(373.3, 135.18) * mm});
            skCircle(sketch, "E72", {"center": v(383.3, 135.18) * mm, "radius": 10 * mm});
            skLineSegment(sketch, "E73.trimOffspring", {"start": v(383.3, 135.18) * mm, "end": v(398.3, 135.18) * mm});
            skSolve(sketch);
        }
        {
            var Q0;
            {var subQ0=sQuery(id+"F54.wireOp",EDGE,"E72");var subQ1=makeQuery(id+"F54.imprint","INTERSECT",VERTEX,{"derivedFrom":[sQuery(id+"F54.wireOp",EDGE,"E71"),subQ0]});Q0=makeQuery(id+"F54.imprint","IMPRINT",FACE,{"disambiguationData":[TD([[makeQuery(id+"F54.imprint","IMPRINT",EDGE,{"disambiguationData":[TD([[subQ1,1.0]])],"derivedFrom":subQ0}),1.0]])]});}
            extrude(context, id + "F55", {"entities" : qUnion([Q0]), "operationType" : NewBodyOperationType.ADD, "depth" : 75 * mm, "offsetDistance" : 25 * mm});
        }
        {
            var Q0;
            Q0=qCreatedBy(makeId("Top.planeOp"),FACE);
            var sketch = newSketch(context, id + "F56", { "sketchPlane" : qUnion([Q0])});
            skLineSegment(sketch, "E74.bottom", {"start": v(911.93, 310.5) * mm, "end": v(711.93, 310.5) * mm});
            skLineSegment(sketch, "E74.top", {"start": v(911.93, 360.5) * mm, "end": v(711.93, 360.5) * mm});
            skLineSegment(sketch, "E74.left", {"start": v(911.93, 310.5) * mm, "end": v(911.93, 360.5) * mm});
            skLineSegment(sketch, "E74.right", {"start": v(711.93, 310.5) * mm, "end": v(711.93, 360.5) * mm});
            skSolve(sketch);
        }
        {
            var Q0;
            Q0=makeQuery(id+"F56.imprint","IMPRINT",FACE,{"disambiguationData":[TD([[makeQuery(id+"F56.imprint","IMPRINT",EDGE,{"derivedFrom":sQuery(id+"F56.wireOp",EDGE,"E74.bottom")}),-1.0]])]});
            extrude(context, id + "F57", {"entities" : qUnion([Q0]), "depth" : 200 * mm, "offsetDistance" : 25 * mm});
        }
        {
            var Q0;
            Q0=makeQuery(id+"F57.opExtrude","SWEPT_FACE",FACE,{"disambiguationData":[OSD([sQuery(id+"F56.wireOp",EDGE,"E74.bottom")])]});
            var sketch = newSketch(context, id + "F58", { "sketchPlane" : qUnion([Q0])});
            skLineSegment(sketch, "E75", {"start": v(811.93, 200) * mm, "end": v(811.93, 165) * mm});
            skCircle(sketch, "E76", {"center": v(811.93, 165) * mm, "radius": 10 * mm});
            skSolve(sketch);
        }
        {
            var Q0;
            Q0 = qSketchRegion(id + "F58", true);
            extrude(context, id + "F59", {"entities" : qUnion([Q0]), "operationType" : NewBodyOperationType.REMOVE, "oppositeDirection" : true, "depth" : 25 * mm, "offsetDistance" : 25 * mm});
        }
        {
            var Q0;
            Q0=makeQuery(id+"F57.opExtrude","SWEPT_BODY",BODY,{"disambiguationData":[OSD([sQuery(id+"F56.wireOp",EDGE,"E74.bottom"),sQuery(id+"F56.wireOp",EDGE,"E74.top"),sQuery(id+"F56.wireOp",EDGE,"E74.left"),sQuery(id+"F56.wireOp",EDGE,"E74.right")])]});
            var Q1;
            Q1=qCreatedBy(makeId("Front.planeOp"),FACE);
            mirror(context, id + "F60", {"entities" : qUnion([Q0]), "mirrorPlane" : qUnion([Q1])});
        }
        {
            var Q0;
            Q0=makeQuery(id+"F55.opExtrude","CAP_FACE",FACE,{"disambiguationData":[OSD([sQuery(id+"F54.wireOp",EDGE,"E72")])],"isStart":false});
            var sketch = newSketch(context, id + "F61", { "sketchPlane" : qUnion([Q0])});
            skCircle(sketch, "E77", {"center": v(383.3, 135.18) * mm, "radius": 7.5 * mm});
            skLineSegment(sketch, "E78", {"start": v(383.3, 135.18) * mm, "end": v(383.3, 145.18) * mm});
            skLineSegment(sketch, "E79", {"start": v(383.3, 142.68) * mm, "end": v(382.3, 142.68) * mm});
            skLineSegment(sketch, "E80", {"start": v(382.3, 142.68) * mm, "end": v(381.34, 145) * mm});
            skLineSegment(sketch, "E81.MirrorCS", {"start": v(383.3, 142.68) * mm, "end": v(384.3, 142.68) * mm});
            skLineSegment(sketch, "E82.MirrorCS", {"start": v(384.3, 142.68) * mm, "end": v(385.26, 145) * mm});
            skSolve(sketch);
        }
        {
            var Q0;
            {var subQ3=sQuery(id+"F61.wireOp",EDGE,"E79");Q0=makeQuery(id+"F61.imprint","IMPRINT",FACE,{"disambiguationData":[TD([[makeQuery(id+"F61.imprint","IMPRINT",EDGE,{"derivedFrom":subQ3}),-1.0]])]});}
            var Q1;
            {var subQ3=sQuery(id+"F61.wireOp",EDGE,"E81.MirrorCS");Q1=makeQuery(id+"F61.imprint","IMPRINT",FACE,{"disambiguationData":[TD([[makeQuery(id+"F61.imprint","IMPRINT",EDGE,{"derivedFrom":subQ3}),1.0]])]});}
            extrude(context, id + "F62", {"entities" : qUnion([Q0, Q1]), "operationType" : NewBodyOperationType.REMOVE, "oppositeDirection" : true, "depth" : 10 * mm, "offsetDistance" : 25 * mm});
        }
        {
            var Q0;
            Q0=makeQuery(id+"F62.boolean.opBoolean","COPY",FACE,{"derivedFrom":makeQuery(id+"F62.opExtrude","SWEPT_FACE",FACE,{"disambiguationData":[OSD([sQuery(id+"F61.wireOp",EDGE,"E79"),sQuery(id+"F61.wireOp",EDGE,"E81.MirrorCS")])]})});
            var Q1;
            Q1=makeQuery(id+"F62.boolean.opBoolean","COPY",FACE,{"derivedFrom":makeQuery(id+"F62.opExtrude","SWEPT_FACE",FACE,{"disambiguationData":[OSD([sQuery(id+"F61.wireOp",EDGE,"E80")])]})});
            var Q2;
            Q2=makeQuery(id+"F62.boolean.opBoolean","COPY",FACE,{"derivedFrom":makeQuery(id+"F62.opExtrude","SWEPT_FACE",FACE,{"disambiguationData":[OSD([sQuery(id+"F61.wireOp",EDGE,"E82.MirrorCS")])]})});
            var Q3;
            Q3=makeQuery(id+"F62.boolean.opBoolean","COPY",FACE,{"derivedFrom":makeQuery(id+"F62.opExtrude","CAP_FACE",FACE,{"disambiguationData":[OSD([sQuery(id+"F54.wireOp",EDGE,"E72"),sQuery(id+"F61.wireOp",EDGE,"E79"),sQuery(id+"F61.wireOp",EDGE,"E80"),sQuery(id+"F61.wireOp",EDGE,"E81.MirrorCS"),sQuery(id+"F61.wireOp",EDGE,"E82.MirrorCS")])],"isStart":false})});
            var Q4;
            Q4=makeQuery(id+"F55.opExtrude","SWEPT_FACE",FACE,{"disambiguationData":[OSD([sQuery(id+"F54.wireOp",EDGE,"E72")])]});
            circularPattern(context, id + "F63", {"patternType" : PatternType.FACE, "faces" : qUnion([Q0, Q1, Q2, Q3]), "axis" : qUnion([Q4]), "angle" : 360 * degree, "instanceCount" : 24, "equalSpace" : true});
        }
        {
            var Q0;
            Q0=qCreatedBy(makeId("Front.planeOp"),FACE);
            var sketch = newSketch(context, id + "F64", { "sketchPlane" : qUnion([Q0])});
            skCircle(sketch, "E83", {"center": v(201.03, 110.05) * mm, "radius": 37.5 * mm});
            skSolve(sketch);
        }
        {
            var Q0;
            Q0=makeQuery(id+"F64.imprint","IMPRINT",FACE,{"disambiguationData":[TD([[makeQuery(id+"F64.imprint","IMPRINT",EDGE,{"derivedFrom":sQuery(id+"F64.wireOp",EDGE,"E83")}),1.0]])]});
            extrude(context, id + "F65", {"entities" : qUnion([Q0]), "depth" : 40 * mm, "offsetDistance" : 25 * mm});
        }
        {
            var Q0;
            Q0=makeQuery(id+"F65.opExtrude","CAP_FACE",FACE,{"disambiguationData":[OSD([sQuery(id+"F64.wireOp",EDGE,"E83")])],"isStart":true});
            var sketch = newSketch(context, id + "F66", { "sketchPlane" : qUnion([Q0])});
            skCircle(sketch, "E84", {"center": v(-201.03, 110.05) * mm, "radius": 35 * mm});
            skLineSegment(sketch, "E85", {"start": v(-201.03, 110.05) * mm, "end": v(-201.03, 147.55) * mm});
            skLineSegment(sketch, "E86", {"start": v(-201.03, 145.05) * mm, "end": v(-202.03, 145.05) * mm});
            skLineSegment(sketch, "E87", {"start": v(-202.03, 145.05) * mm, "end": v(-203.05, 147.5) * mm});
            skLineSegment(sketch, "E88.MirrorCS", {"start": v(-200.03, 145.05) * mm, "end": v(-199.02, 147.5) * mm});
            skLineSegment(sketch, "E89.MirrorCS", {"start": v(-201.03, 145.05) * mm, "end": v(-200.03, 145.05) * mm});
            skSolve(sketch);
        }
        {
            var Q0;
            {var subQ3=sQuery(id+"F66.wireOp",EDGE,"E86");Q0=makeQuery(id+"F66.imprint","IMPRINT",FACE,{"disambiguationData":[TD([[makeQuery(id+"F66.imprint","IMPRINT",EDGE,{"derivedFrom":subQ3}),-1.0]])]});}
            var Q1;
            {var subQ4=sQuery(id+"F66.wireOp",EDGE,"E88.MirrorCS");Q1=makeQuery(id+"F66.imprint","IMPRINT",FACE,{"disambiguationData":[TD([[makeQuery(id+"F66.imprint","IMPRINT",EDGE,{"derivedFrom":subQ4}),1.0]])]});}
            extrude(context, id + "F67", {"entities" : qUnion([Q0, Q1]), "operationType" : NewBodyOperationType.REMOVE, "oppositeDirection" : true, "depth" : 15 * mm, "offsetDistance" : 25 * mm});
        }
        {
            var Q0;
            Q0=makeQuery(id+"F67.boolean.opBoolean","COPY",FACE,{"derivedFrom":makeQuery(id+"F67.opExtrude","SWEPT_FACE",FACE,{"disambiguationData":[OSD([sQuery(id+"F66.wireOp",EDGE,"E86"),sQuery(id+"F66.wireOp",EDGE,"E89.MirrorCS")])]})});
            var Q1;
            Q1=makeQuery(id+"F67.boolean.opBoolean","COPY",FACE,{"derivedFrom":makeQuery(id+"F67.opExtrude","SWEPT_FACE",FACE,{"disambiguationData":[OSD([sQuery(id+"F66.wireOp",EDGE,"E88.MirrorCS")])]})});
            var Q2;
            Q2=makeQuery(id+"F67.boolean.opBoolean","COPY",FACE,{"derivedFrom":makeQuery(id+"F67.opExtrude","CAP_FACE",FACE,{"disambiguationData":[OSD([sQuery(id+"F64.wireOp",EDGE,"E83"),sQuery(id+"F66.wireOp",EDGE,"E86"),sQuery(id+"F66.wireOp",EDGE,"E87"),sQuery(id+"F66.wireOp",EDGE,"E88.MirrorCS"),sQuery(id+"F66.wireOp",EDGE,"E89.MirrorCS")])],"isStart":false})});
            var Q3;
            Q3=makeQuery(id+"F67.boolean.opBoolean","COPY",FACE,{"derivedFrom":makeQuery(id+"F67.opExtrude","SWEPT_FACE",FACE,{"disambiguationData":[OSD([sQuery(id+"F66.wireOp",EDGE,"E87")])]})});
            var Q4;
            Q4=makeQuery(id+"F65.opExtrude","SWEPT_FACE",FACE,{"disambiguationData":[OSD([sQuery(id+"F64.wireOp",EDGE,"E83")])]});
            circularPattern(context, id + "F68", {"patternType" : PatternType.FACE, "faces" : qUnion([Q0, Q1, Q2, Q3]), "axis" : qUnion([Q4]), "angle" : 360 * degree, "instanceCount" : 44, "equalSpace" : true});
        }
        {
            var Q0;
            Q0=makeQuery(id+"F65.opExtrude","CAP_FACE",FACE,{"disambiguationData":[OSD([sQuery(id+"F64.wireOp",EDGE,"E83")])],"isStart":false});
            var sketch = newSketch(context, id + "F69", { "sketchPlane" : qUnion([Q0])});
            skCircle(sketch, "E90", {"center": v(201.03, 110.05) * mm, "radius": 50 * mm});
            skSolve(sketch);
        }
        {
            var Q0;
            Q0 = qSketchRegion(id + "F69", true);
            extrude(context, id + "F70", {"entities" : qUnion([Q0]), "operationType" : NewBodyOperationType.ADD, "oppositeDirection" : true, "depth" : 25 * mm, "offsetDistance" : 25 * mm});
        }
        {
            var Q0;
            Q0=makeQuery(id+"F70.boolean.opBoolean","MERGE",FACE,{"derivedFrom":[makeQuery(id+"F65.opExtrude","CAP_FACE",FACE,{"disambiguationData":[OSD([sQuery(id+"F64.wireOp",EDGE,"E83")])],"isStart":false}),makeQuery(id+"F70.opExtrude","CAP_FACE",FACE,{"disambiguationData":[OSD([sQuery(id+"F69.wireOp",EDGE,"E90")])],"isStart":true})]});
            var sketch = newSketch(context, id + "F71", { "sketchPlane" : qUnion([Q0])});
            skCircle(sketch, "E91", {"center": v(201.03, 110.05) * mm, "radius": 37.5 * mm});
            skLineSegment(sketch, "E92", {"start": v(201.03, 110.05) * mm, "end": v(201.03, 160.05) * mm});
            skLineSegment(sketch, "E93", {"start": v(201.03, 147.55) * mm, "end": v(196.03, 147.55) * mm});
            skLineSegment(sketch, "E94", {"start": v(196.03, 147.55) * mm, "end": v(191.26, 159.09) * mm});
            skLineSegment(sketch, "E95.MirrorCS", {"start": v(201.03, 147.55) * mm, "end": v(206.03, 147.55) * mm});
            skLineSegment(sketch, "E96.MirrorCS", {"start": v(206.03, 147.55) * mm, "end": v(210.81, 159.09) * mm});
            skSolve(sketch);
        }
        {
            var Q0;
            {var subQ3=sQuery(id+"F71.wireOp",EDGE,"E93");Q0=makeQuery(id+"F71.imprint","IMPRINT",FACE,{"disambiguationData":[TD([[makeQuery(id+"F71.imprint","IMPRINT",EDGE,{"derivedFrom":subQ3}),-1.0]])]});}
            var Q1;
            {var subQ3=sQuery(id+"F71.wireOp",EDGE,"E95.MirrorCS");Q1=makeQuery(id+"F71.imprint","IMPRINT",FACE,{"disambiguationData":[TD([[makeQuery(id+"F71.imprint","IMPRINT",EDGE,{"derivedFrom":subQ3}),1.0]])]});}
            extrude(context, id + "F72", {"entities" : qUnion([Q0, Q1]), "operationType" : NewBodyOperationType.REMOVE, "oppositeDirection" : true, "depth" : 25 * mm, "offsetDistance" : 25 * mm});
        }
        {
            var Q0;
            Q0=makeQuery(id+"F72.boolean.opBoolean","COPY",FACE,{"derivedFrom":makeQuery(id+"F72.opExtrude","SWEPT_FACE",FACE,{"disambiguationData":[OSD([sQuery(id+"F71.wireOp",EDGE,"E93"),sQuery(id+"F71.wireOp",EDGE,"E95.MirrorCS")])]})});
            var Q1;
            Q1=makeQuery(id+"F72.boolean.opBoolean","COPY",FACE,{"derivedFrom":makeQuery(id+"F72.opExtrude","SWEPT_FACE",FACE,{"disambiguationData":[OSD([sQuery(id+"F71.wireOp",EDGE,"E96.MirrorCS")])]})});
            var Q2;
            Q2=makeQuery(id+"F72.boolean.opBoolean","COPY",FACE,{"derivedFrom":makeQuery(id+"F72.opExtrude","SWEPT_FACE",FACE,{"disambiguationData":[OSD([sQuery(id+"F71.wireOp",EDGE,"E94")])]})});
            var Q3;
            Q3=makeQuery(id+"F70.opExtrude","SWEPT_FACE",FACE,{"disambiguationData":[OSD([sQuery(id+"F69.wireOp",EDGE,"E90")])]});
            circularPattern(context, id + "F73", {"patternType" : PatternType.FACE, "faces" : qUnion([Q0, Q1, Q2]), "axis" : qUnion([Q3]), "angle" : 360 * degree, "instanceCount" : 24, "equalSpace" : true});
        }
        {
            var Q0;
            Q0=makeQuery(id+"F70.boolean.opBoolean","MERGE",FACE,{"derivedFrom":[makeQuery(id+"F65.opExtrude","CAP_FACE",FACE,{"disambiguationData":[OSD([sQuery(id+"F64.wireOp",EDGE,"E83")])],"isStart":false}),makeQuery(id+"F70.opExtrude","CAP_FACE",FACE,{"disambiguationData":[OSD([sQuery(id+"F69.wireOp",EDGE,"E90")])],"isStart":true})]});
            var sketch = newSketch(context, id + "F74", { "sketchPlane" : qUnion([Q0])});
            skLineSegment(sketch, "E97", {"start": v(163.53, 110.05) * mm, "end": v(238.53, 110.05) * mm});
            skCircle(sketch, "E98", {"center": v(201.03, 110.05) * mm, "radius": 6.25 * mm});
            skSolve(sketch);
        }
        {
            var Q0;
            {var subQ0=sQuery(id+"F74.wireOp",EDGE,"E98");var subQ1=sQuery(id+"F74.wireOp",EDGE,"E97");var subQ2=makeQuery(id+"F74.imprint","INTERSECT",VERTEX,{"disambiguationData":[OD(0.0)],"derivedFrom":[subQ1,subQ0]});Q0=makeQuery(id+"F74.imprint","IMPRINT",FACE,{"disambiguationData":[TD([[makeQuery(id+"F74.imprint","IMPRINT",EDGE,{"disambiguationData":[TD([[subQ2,-1.0]])],"derivedFrom":subQ1}),-1.0]])]});}
            var Q1;
            {var subQ0=sQuery(id+"F74.wireOp",EDGE,"E98");var subQ1=sQuery(id+"F74.wireOp",EDGE,"E97");var subQ2=makeQuery(id+"F74.imprint","INTERSECT",VERTEX,{"disambiguationData":[OD(0.0)],"derivedFrom":[subQ1,subQ0]});Q1=makeQuery(id+"F74.imprint","IMPRINT",FACE,{"disambiguationData":[TD([[makeQuery(id+"F74.imprint","IMPRINT",EDGE,{"disambiguationData":[TD([[subQ2,-1.0]])],"derivedFrom":subQ1}),1.0]])]});}
            extrude(context, id + "F75", {"entities" : qUnion([Q0, Q1]), "operationType" : NewBodyOperationType.REMOVE, "oppositeDirection" : true, "depth" : 73.5 * mm, "offsetDistance" : 25 * mm});
        }
        {
            var Q0;
            Q0=makeQuery(id+"F60.opPattern","COPY",FACE,{"derivedFrom":makeQuery(id+"F59.boolean.opBoolean","COPY",FACE,{"derivedFrom":makeQuery(id+"F59.opExtrude","CAP_FACE",FACE,{"disambiguationData":[OSD([sQuery(id+"F58.wireOp",EDGE,"E76")])],"isStart":false})}),"instanceName":"1"});
            var sketch = newSketch(context, id + "F76", { "sketchPlane" : qUnion([Q0])});
            skCircle(sketch, "E99", {"center": v(-811.93, 165) * mm, "radius": 10 * mm});
            skSolve(sketch);
        }
        {
            var Q0;
            Q0=makeQuery(id+"F76.imprint","IMPRINT",FACE,{"disambiguationData":[TD([[makeQuery(id+"F76.imprint","IMPRINT",EDGE,{"derivedFrom":sQuery(id+"F76.wireOp",EDGE,"E99")}),-1.0]])]});
            extrude(context, id + "F77", {"entities" : qUnion([Q0]), "operationType" : NewBodyOperationType.REMOVE, "oppositeDirection" : true, "depth" : 127 * mm, "offsetDistance" : 25 * mm});
        }
        {
            var Q0;
            Q0=makeQuery(id+"F57.opExtrude","CAP_FACE",FACE,{"disambiguationData":[OSD([sQuery(id+"F56.wireOp",EDGE,"E74.bottom"),sQuery(id+"F56.wireOp",EDGE,"E74.top"),sQuery(id+"F56.wireOp",EDGE,"E74.left"),sQuery(id+"F56.wireOp",EDGE,"E74.right")])],"isStart":false});
            var sketch = newSketch(context, id + "F78", { "sketchPlane" : qUnion([Q0])});
            skLineSegment(sketch, "E100", {"start": v(811.93, 310.5) * mm, "end": v(811.93, 360.5) * mm});
            skLineSegment(sketch, "E101", {"start": v(811.93, 360.5) * mm, "end": v(771.93, 360.5) * mm});
            skLineSegment(sketch, "E102", {"start": v(771.93, 360.5) * mm, "end": v(771.93, 310.5) * mm});
            skLineSegment(sketch, "E103.MirrorCS", {"start": v(851.93, 360.5) * mm, "end": v(851.93, 310.5) * mm});
            skSolve(sketch);
        }
        {
            var Q0;
            {var subQ0=sQuery(id+"F78.wireOp",EDGE,"E102");Q0=makeQuery(id+"F78.imprint","IMPRINT",FACE,{"disambiguationData":[TD([[makeQuery(id+"F78.imprint","IMPRINT",EDGE,{"derivedFrom":subQ0}),-1.0]])]});}
            var Q1;
            {var subQ0=sQuery(id+"F78.wireOp",EDGE,"E103.MirrorCS");Q1=makeQuery(id+"F78.imprint","IMPRINT",FACE,{"disambiguationData":[TD([[makeQuery(id+"F78.imprint","IMPRINT",EDGE,{"derivedFrom":subQ0}),1.0]])]});}
            extrude(context, id + "F79", {"entities" : qUnion([Q0, Q1]), "operationType" : NewBodyOperationType.REMOVE, "oppositeDirection" : true, "depth" : 180 * mm, "offsetDistance" : 25 * mm});
        }
        {
            var Q0;
            Q0=makeQuery(id+"F60.opPattern","COPY",FACE,{"derivedFrom":makeQuery(id+"F57.opExtrude","CAP_FACE",FACE,{"disambiguationData":[OSD([sQuery(id+"F56.wireOp",EDGE,"E74.bottom"),sQuery(id+"F56.wireOp",EDGE,"E74.top"),sQuery(id+"F56.wireOp",EDGE,"E74.left"),sQuery(id+"F56.wireOp",EDGE,"E74.right")])],"isStart":false}),"instanceName":"1"});
            var sketch = newSketch(context, id + "F80", { "sketchPlane" : qUnion([Q0])});
            skLineSegment(sketch, "E104", {"start": v(811.93, -360.5) * mm, "end": v(811.93, -310.5) * mm});
            skLineSegment(sketch, "E105", {"start": v(811.93, -310.5) * mm, "end": v(771.93, -310.5) * mm});
            skLineSegment(sketch, "E106", {"start": v(771.93, -310.5) * mm, "end": v(771.93, -360.5) * mm});
            skLineSegment(sketch, "E107.MirrorCS", {"start": v(851.93, -310.5) * mm, "end": v(851.93, -360.5) * mm});
            skSolve(sketch);
        }
        {
            var Q0;
            {var subQ0=sQuery(id+"F80.wireOp",EDGE,"E106");Q0=makeQuery(id+"F80.imprint","IMPRINT",FACE,{"disambiguationData":[TD([[makeQuery(id+"F80.imprint","IMPRINT",EDGE,{"derivedFrom":subQ0}),-1.0]])]});}
            var Q1;
            {var subQ0=sQuery(id+"F80.wireOp",EDGE,"E107.MirrorCS");Q1=makeQuery(id+"F80.imprint","IMPRINT",FACE,{"disambiguationData":[TD([[makeQuery(id+"F80.imprint","IMPRINT",EDGE,{"derivedFrom":subQ0}),1.0]])]});}
            extrude(context, id + "F81", {"entities" : qUnion([Q0, Q1]), "operationType" : NewBodyOperationType.REMOVE, "oppositeDirection" : true, "depth" : 180 * mm, "offsetDistance" : 25 * mm});
        }
        {
            var Q0;
            Q0=makeQuery(id+"F81.boolean.opBoolean","COPY",EDGE,{"derivedFrom":makeQuery(id+"F81.opExtrude","CAP_EDGE",EDGE,{"disambiguationData":[OSD([sQuery(id+"F80.wireOp",EDGE,"E107.MirrorCS")])],"isStart":false})});
            var Q1;
            Q1=makeQuery(id+"F81.boolean.opBoolean","COPY",EDGE,{"derivedFrom":makeQuery(id+"F81.opExtrude","CAP_EDGE",EDGE,{"disambiguationData":[OSD([sQuery(id+"F80.wireOp",EDGE,"E106")])],"isStart":false})});
            var Q2;
            Q2=makeQuery(id+"F81.boolean.opBoolean","COPY",EDGE,{"derivedFrom":makeQuery(id+"F81.opExtrude","CAP_EDGE",EDGE,{"disambiguationData":[OSD([sQuery(id+"F80.wireOp",EDGE,"E106")])],"isStart":true})});
            var Q3;
            Q3=makeQuery(id+"F81.boolean.opBoolean","COPY",EDGE,{"derivedFrom":makeQuery(id+"F81.opExtrude","CAP_EDGE",EDGE,{"disambiguationData":[OSD([sQuery(id+"F80.wireOp",EDGE,"E107.MirrorCS")])],"isStart":true})});
            var Q4;
            Q4=makeQuery(id+"F79.boolean.opBoolean","COPY",EDGE,{"derivedFrom":makeQuery(id+"F79.opExtrude","CAP_EDGE",EDGE,{"disambiguationData":[OSD([sQuery(id+"F78.wireOp",EDGE,"E102")])],"isStart":false})});
            var Q5;
            Q5=makeQuery(id+"F79.boolean.opBoolean","COPY",EDGE,{"derivedFrom":makeQuery(id+"F79.opExtrude","CAP_EDGE",EDGE,{"disambiguationData":[OSD([sQuery(id+"F78.wireOp",EDGE,"E102")])],"isStart":true})});
            var Q6;
            Q6=makeQuery(id+"F79.boolean.opBoolean","COPY",EDGE,{"derivedFrom":makeQuery(id+"F79.opExtrude","CAP_EDGE",EDGE,{"disambiguationData":[OSD([sQuery(id+"F78.wireOp",EDGE,"E103.MirrorCS")])],"isStart":true})});
            var Q7;
            Q7=makeQuery(id+"F79.boolean.opBoolean","COPY",EDGE,{"derivedFrom":makeQuery(id+"F79.opExtrude","CAP_EDGE",EDGE,{"disambiguationData":[OSD([sQuery(id+"F78.wireOp",EDGE,"E103.MirrorCS")])],"isStart":false})});
            fillet(context, id + "F82", {"entities" : qUnion([Q0, Q1, Q2, Q3, Q4, Q5, Q6, Q7]), "radius" : 10 * mm, "tangentPropagation" : true, "allowEdgeOverflow" : false});
        }
        {
            var Q0;
            Q0=makeQuery(id+"F60.opPattern","COPY",EDGE,{"derivedFrom":makeQuery(id+"F57.opExtrude","SWEPT_EDGE",EDGE,{"disambiguationData":[OSD([sQuery(id+"F56.wireOp",EDGE,"E74.top"),sQuery(id+"F56.wireOp",EDGE,"E74.right")])]}),"instanceName":"1"});
            var Q1;
            Q1=makeQuery(id+"F60.opPattern","COPY",EDGE,{"derivedFrom":makeQuery(id+"F57.opExtrude","SWEPT_EDGE",EDGE,{"disambiguationData":[OSD([sQuery(id+"F56.wireOp",EDGE,"E74.top"),sQuery(id+"F56.wireOp",EDGE,"E74.left")])]}),"instanceName":"1"});
            var Q2;
            Q2=makeQuery(id+"F60.opPattern","COPY",EDGE,{"derivedFrom":makeQuery(id+"F57.opExtrude","SWEPT_EDGE",EDGE,{"disambiguationData":[OSD([sQuery(id+"F56.wireOp",EDGE,"E74.bottom"),sQuery(id+"F56.wireOp",EDGE,"E74.left")])]}),"instanceName":"1"});
            var Q3;
            Q3=makeQuery(id+"F60.opPattern","COPY",EDGE,{"derivedFrom":makeQuery(id+"F57.opExtrude","SWEPT_EDGE",EDGE,{"disambiguationData":[OSD([sQuery(id+"F56.wireOp",EDGE,"E74.bottom"),sQuery(id+"F56.wireOp",EDGE,"E74.right")])]}),"instanceName":"1"});
            var Q4;
            Q4=makeQuery(id+"F57.opExtrude","SWEPT_EDGE",EDGE,{"disambiguationData":[OSD([sQuery(id+"F56.wireOp",EDGE,"E74.top"),sQuery(id+"F56.wireOp",EDGE,"E74.right")])]});
            var Q5;
            Q5=makeQuery(id+"F57.opExtrude","SWEPT_EDGE",EDGE,{"disambiguationData":[OSD([sQuery(id+"F56.wireOp",EDGE,"E74.bottom"),sQuery(id+"F56.wireOp",EDGE,"E74.right")])]});
            var Q6;
            Q6=makeQuery(id+"F57.opExtrude","SWEPT_EDGE",EDGE,{"disambiguationData":[OSD([sQuery(id+"F56.wireOp",EDGE,"E74.top"),sQuery(id+"F56.wireOp",EDGE,"E74.left")])]});
            var Q7;
            Q7=makeQuery(id+"F57.opExtrude","SWEPT_EDGE",EDGE,{"disambiguationData":[OSD([sQuery(id+"F56.wireOp",EDGE,"E74.bottom"),sQuery(id+"F56.wireOp",EDGE,"E74.left")])]});
            chamfer(context, id + "F83", {"entities" : qUnion([Q0, Q1, Q2, Q3, Q4, Q5, Q6, Q7]), "width" : 5 * mm, "tangentPropagation" : true});
        }
        {
            var Q0;
            Q0=makeQuery(id+"F60.opPattern","COPY",FACE,{"derivedFrom":makeQuery(id+"F57.opExtrude","CAP_FACE",FACE,{"disambiguationData":[OSD([sQuery(id+"F56.wireOp",EDGE,"E74.bottom"),sQuery(id+"F56.wireOp",EDGE,"E74.top"),sQuery(id+"F56.wireOp",EDGE,"E74.left"),sQuery(id+"F56.wireOp",EDGE,"E74.right")])],"isStart":true}),"instanceName":"1"});
            var sketch = newSketch(context, id + "F84", { "sketchPlane" : qUnion([Q0])});
            skLineSegment(sketch, "E108", {"start": v(711.93, 335.5) * mm, "end": v(736.93, 335.5) * mm});
            skLineSegment(sketch, "E109", {"start": v(811.93, 360.5) * mm, "end": v(811.93, 323.88) * mm});
            skCircle(sketch, "E110", {"center": v(736.93, 335.5) * mm, "radius": 10 * mm});
            skCircle(sketch, "E111.MirrorC", {"center": v(886.93, 335.5) * mm, "radius": 10 * mm});
            skSolve(sketch);
        }
        {
            var Q0;
            Q0=makeQuery(id+"F84.imprint","IMPRINT",FACE,{"disambiguationData":[TD([[makeQuery(id+"F84.imprint","IMPRINT",EDGE,{"derivedFrom":sQuery(id+"F84.wireOp",EDGE,"E110")}),1.0]])]});
            var Q1;
            Q1=makeQuery(id+"F84.imprint","IMPRINT",FACE,{"disambiguationData":[TD([[makeQuery(id+"F84.imprint","IMPRINT",EDGE,{"derivedFrom":sQuery(id+"F84.wireOp",EDGE,"E111.MirrorC")}),-1.0]])]});
            extrude(context, id + "F85", {"entities" : qUnion([Q0, Q1]), "operationType" : NewBodyOperationType.REMOVE, "oppositeDirection" : true, "depth" : 25 * mm, "offsetDistance" : 25 * mm});
        }
        {
            var Q0;
            Q0=makeQuery(id+"F57.opExtrude","CAP_FACE",FACE,{"disambiguationData":[OSD([sQuery(id+"F56.wireOp",EDGE,"E74.bottom"),sQuery(id+"F56.wireOp",EDGE,"E74.top"),sQuery(id+"F56.wireOp",EDGE,"E74.left"),sQuery(id+"F56.wireOp",EDGE,"E74.right")])],"isStart":true});
            var sketch = newSketch(context, id + "F86", { "sketchPlane" : qUnion([Q0])});
            skLineSegment(sketch, "E112", {"start": v(711.93, -335.5) * mm, "end": v(736.93, -335.5) * mm});
            skCircle(sketch, "E113", {"center": v(736.93, -335.5) * mm, "radius": 10 * mm});
            skLineSegment(sketch, "E114", {"start": v(811.93, -310.5) * mm, "end": v(811.93, -323.91) * mm});
            skCircle(sketch, "E115.MirrorC", {"center": v(886.93, -335.5) * mm, "radius": 10 * mm});
            skSolve(sketch);
        }
        {
            var Q0;
            Q0 = qSketchRegion(id + "F86", true);
            extrude(context, id + "F87", {"entities" : qUnion([Q0]), "operationType" : NewBodyOperationType.REMOVE, "oppositeDirection" : true, "depth" : 25 * mm, "offsetDistance" : 25 * mm});
        }
    });
